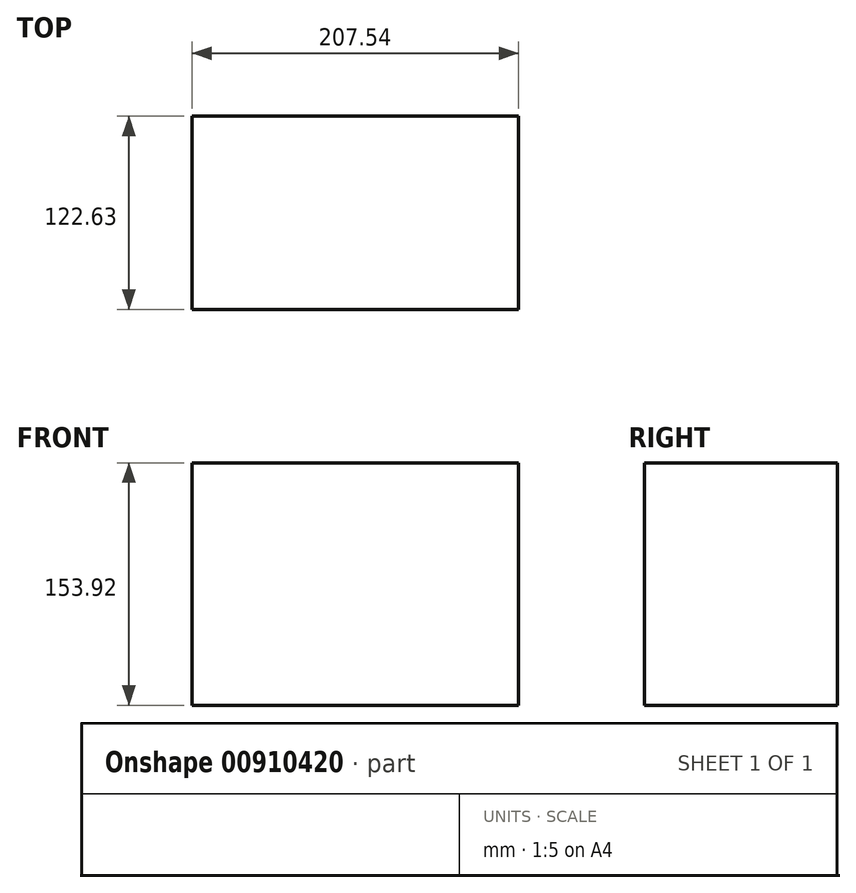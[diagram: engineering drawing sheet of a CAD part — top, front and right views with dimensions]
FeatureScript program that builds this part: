
annotation { "Feature Type Name" : "Feature", "Feature Type Description" : "" }
export const myFeature = defineFeature(function(context is Context, id is Id, definition is map)
    precondition{}
    {
        {
            var Q0;
            Q0=qCreatedBy(makeId("Top.planeOp"),FACE);
            var sketch = newSketch(context, id + "F0", { "sketchPlane" : qUnion([Q0])});
            skCircle(sketch, "E0", {"center": v(-377.32, 319.9) * mm, "radius": 63.5 * mm});
            skLineSegment(sketch, "E1.bottom", {"start": v(108.5, 232.64) * mm, "end": v(316.03, 232.64) * mm});
            skLineSegment(sketch, "E1.top", {"start": v(108.5, 110) * mm, "end": v(316.03, 110) * mm});
            skLineSegment(sketch, "E1.left", {"start": v(108.5, 232.64) * mm, "end": v(108.5, 110) * mm});
            skLineSegment(sketch, "E1.right", {"start": v(316.03, 232.64) * mm, "end": v(316.03, 110) * mm});
            skLineSegment(sketch, "E2", {"start": v(-335.96, -77.57) * mm, "end": v(-142.58, -143.6) * mm});
            skLineSegment(sketch, "E3", {"start": v(-142.58, -143.6) * mm, "end": v(-142.58, -336.98) * mm});
            skLineSegment(sketch, "E4", {"start": v(-142.58, -336.98) * mm, "end": v(-364.26, -372.36) * mm});
            skLineSegment(sketch, "E5", {"start": v(-364.26, -372.36) * mm, "end": v(-335.96, -77.57) * mm});
            skLineSegment(sketch, "E6", {"start": v(-277, -160.1) * mm, "end": v(-310.02, -292.17) * mm});
            skLineSegment(sketch, "E7", {"start": v(-310.02, -292.17) * mm, "end": v(-239, -309.93) * mm});
            skLineSegment(sketch, "E8", {"start": v(-239, -309.93) * mm, "end": v(-277, -160.1) * mm});
            skSolve(sketch);
        }
        {
            var Q0;
            Q0=makeQuery(id+"F0.imprint","IMPRINT",FACE,{"disambiguationData":[TD([[makeQuery(id+"F0.imprint","IMPRINT",EDGE,{"derivedFrom":sQuery(id+"F0.wireOp",EDGE,"E1.bottom")}),-1.0]])]});
            extrude(context, id + "F1", {"entities" : qUnion([Q0]), "depth" : 153.92 * mm, "offsetDistance" : 25.4 * mm});
        }
    });
